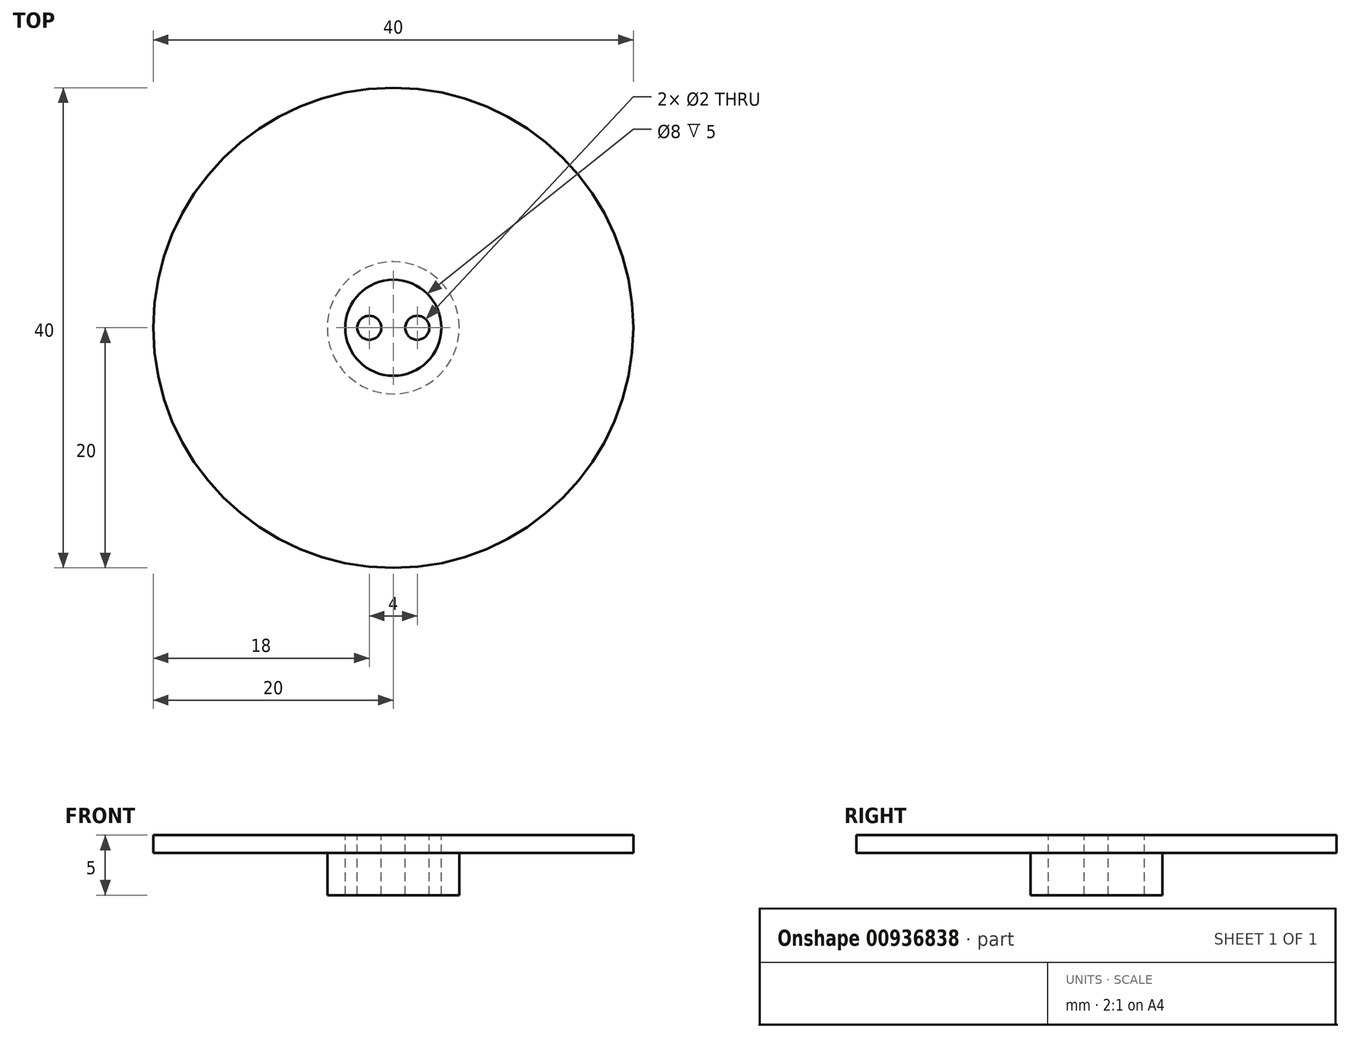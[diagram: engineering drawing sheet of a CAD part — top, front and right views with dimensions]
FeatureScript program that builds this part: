
annotation { "Feature Type Name" : "Feature", "Feature Type Description" : "" }
export const myFeature = defineFeature(function(context is Context, id is Id, definition is map)
    precondition{}
    {
        {
            var Q0;
            Q0=qCreatedBy(makeId("Top.planeOp"),FACE);
            var sketch = newSketch(context, id + "F0", { "sketchPlane" : qUnion([Q0])});
            skCircle(sketch, "E0", {"center": v(0, 0) * mm, "radius": 20 * mm});
            skSolve(sketch);
        }
        {
            var Q0;
            Q0 = qSketchRegion(id + "F0", true);
            extrude(context, id + "F1", {"entities" : qUnion([Q0]), "depth" : 1.5 * mm, "offsetDistance" : 25 * mm});
        }
        {
            var Q0;
            Q0=makeQuery(id+"F1.opExtrude","CAP_FACE",FACE,{"disambiguationData":[OSD([sQuery(id+"F0.wireOp",EDGE,"E0")])],"isStart":false});
            var sketch = newSketch(context, id + "F2", { "sketchPlane" : qUnion([Q0])});
            skCircle(sketch, "E1", {"center": v(0, 0) * mm, "radius": 5.5 * mm});
            skSolve(sketch);
        }
        {
            var Q0;
            Q0 = qSketchRegion(id + "F2", true);
            extrude(context, id + "F3", {"entities" : qUnion([Q0]), "operationType" : NewBodyOperationType.ADD, "oppositeDirection" : true, "depth" : 5 * mm, "offsetDistance" : 25 * mm});
        }
        {
            var Q0;
            Q0=makeQuery(id+"F1.opExtrude","CAP_FACE",FACE,{"disambiguationData":[OSD([sQuery(id+"F0.wireOp",EDGE,"E0")])],"isStart":false});
            var sketch = newSketch(context, id + "F4", { "sketchPlane" : qUnion([Q0])});
            skCircle(sketch, "E2", {"center": v(0, 0) * mm, "radius": 4 * mm});
            skSolve(sketch);
        }
        {
            var Q0;
            Q0 = qSketchRegion(id + "F4", true);
            extrude(context, id + "F5", {"entities" : qUnion([Q0]), "operationType" : NewBodyOperationType.REMOVE, "oppositeDirection" : true, "depth" : 25 * mm, "offsetDistance" : 25 * mm});
        }
        {
            var Q0;
            Q0=makeQuery(id+"F1.opExtrude","CAP_FACE",FACE,{"disambiguationData":[OSD([sQuery(id+"F0.wireOp",EDGE,"E0")])],"isStart":false});
            var sketch = newSketch(context, id + "F6", { "sketchPlane" : qUnion([Q0])});
            skCircle(sketch, "E3", {"center": v(0, 0) * mm, "radius": 4 * mm});
            skSolve(sketch);
        }
        {
            var Q0;
            Q0 = qSketchRegion(id + "F6", true);
            extrude(context, id + "F7", {"entities" : qUnion([Q0]), "oppositeDirection" : true, "depth" : 5 * mm, "offsetDistance" : 25 * mm});
        }
        {
            var Q0;
            Q0=makeQuery(id+"F7.opExtrude","CAP_FACE",FACE,{"disambiguationData":[OSD([sQuery(id+"F6.wireOp",EDGE,"E3")])],"isStart":true});
            var sketch = newSketch(context, id + "F8", { "sketchPlane" : qUnion([Q0])});
            skCircle(sketch, "E4", {"center": v(-2, 0) * mm, "radius": 1 * mm});
            skCircle(sketch, "E5", {"center": v(2, 0) * mm, "radius": 1 * mm});
            skSolve(sketch);
        }
        {
            var Q0;
            Q0 = qSketchRegion(id + "F8", true);
            extrude(context, id + "F9", {"entities" : qUnion([Q0]), "oppositeDirection" : true, "depth" : 8 * mm, "offsetDistance" : 25 * mm});
        }
        {
            var Q0;
            Q0=makeQuery(id+"F9.opExtrude","CAP_FACE",FACE,{"disambiguationData":[OSD([sQuery(id+"F8.wireOp",EDGE,"E4")])],"isStart":false});
            var sketch = newSketch(context, id + "F10", { "sketchPlane" : qUnion([Q0])});
            skArc(sketch, "E6.1.0.0", {"start": v(2.98, 0.2) * mm, "mid": v(2, 1) * mm, "end": v(1.02, 0.2) * mm});
            skLineSegment(sketch, "E6.1.0.1", {"start": v(1.02, 0.2) * mm, "end": v(1.33, 0.2) * mm});
            skLineSegment(sketch, "E6.1.0.2", {"start": v(2.67, 0.2) * mm, "end": v(2.98, 0.2) * mm});
            skArc(sketch, "E6.1.0.3", {"start": v(1.33, 0.2) * mm, "mid": v(2, -0.7) * mm, "end": v(2.67, 0.2) * mm});
            skLineSegment(sketch, "E7", {"start": v(0, 8.27) * mm, "end": v(0, -7.17) * mm, "construction": true});
            skLineSegment(sketch, "E8.MirrorCS", {"start": v(-2.67, 0.2) * mm, "end": v(-2.98, 0.2) * mm});
            skArc(sketch, "E9.MirrorCS", {"start": v(-1.33, 0.2) * mm, "mid": v(-2, -0.7) * mm, "end": v(-2.67, 0.2) * mm});
            skLineSegment(sketch, "E10.MirrorCS", {"start": v(-1.02, 0.2) * mm, "end": v(-1.33, 0.2) * mm});
            skArc(sketch, "E11.MirrorCS", {"start": v(-2.98, 0.2) * mm, "mid": v(-2, 1) * mm, "end": v(-1.02, 0.2) * mm});
            skSolve(sketch);
        }
        {
            var Q0;
            Q0 = qSketchRegion(id + "F10", true);
            extrude(context, id + "F11", {"entities" : qUnion([Q0]), "operationType" : NewBodyOperationType.REMOVE, "oppositeDirection" : true, "depth" : 3 * mm, "offsetDistance" : 25 * mm});
        }
        {
            var Q0;
            Q0 = qSketchRegion(id + "F8", true);
            extrude(context, id + "F12", {"entities" : qUnion([Q0]), "operationType" : NewBodyOperationType.REMOVE, "oppositeDirection" : true, "depth" : 25 * mm, "offsetDistance" : 25 * mm});
        }
        {
            var Q0;
            Q0=qCreatedBy(makeId("Right.planeOp"),FACE);
            var sketch = newSketch(context, id + "F13", { "sketchPlane" : qUnion([Q0])});
            skLineSegment(sketch, "E12.bottom", {"start": v(-1.6, -3.5) * mm, "end": v(0.4, -3.5) * mm});
            skLineSegment(sketch, "E12.top", {"start": v(-1.6, -4) * mm, "end": v(0.4, -4) * mm});
            skLineSegment(sketch, "E12.left", {"start": v(-1.6, -3.5) * mm, "end": v(-1.6, -4) * mm});
            skLineSegment(sketch, "E12.right", {"start": v(0.4, -3.5) * mm, "end": v(0.4, -4) * mm});
            skSolve(sketch);
        }
        {
            var Q0;
            Q0 = qSketchRegion(id + "F13", true);
            extrude(context, id + "F14", {"entities" : qUnion([Q0]), "operationType" : NewBodyOperationType.REMOVE, "endBound" : BoundingType.SYMMETRIC, "depth" : 25 * mm, "offsetDistance" : 25 * mm});
        }
    });
